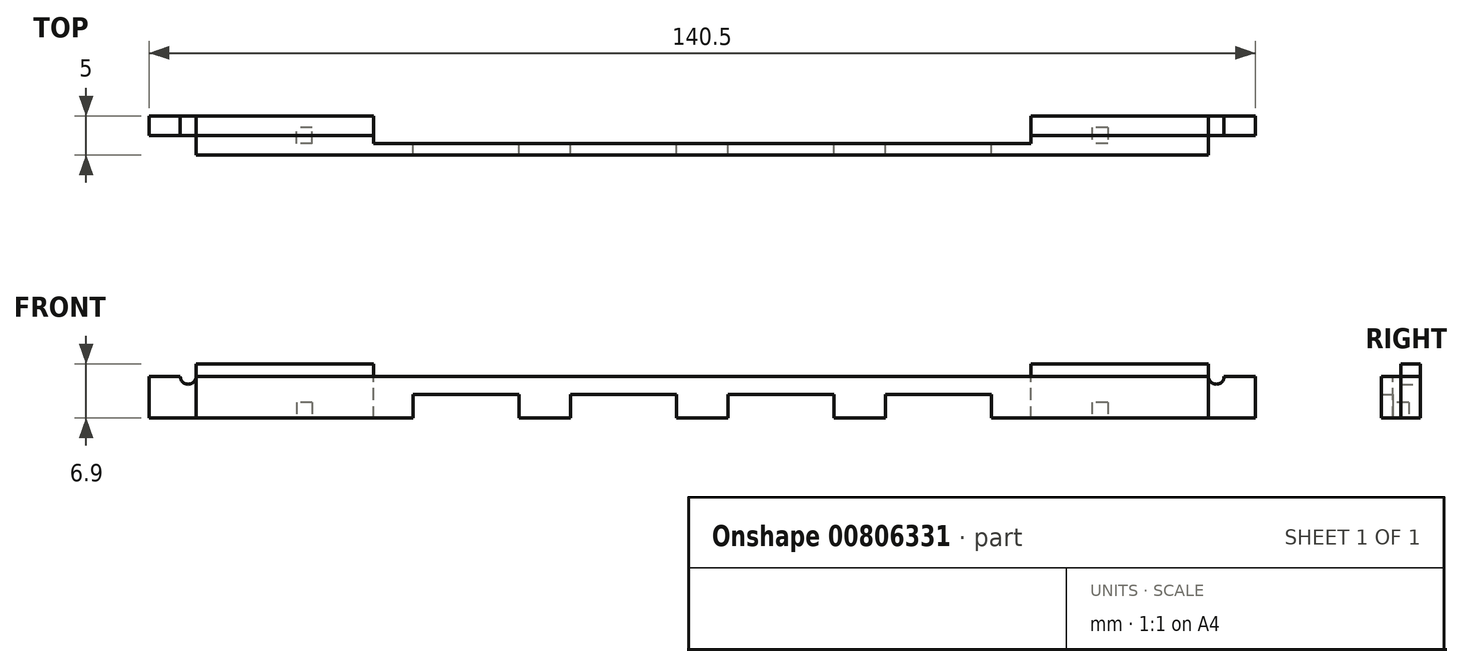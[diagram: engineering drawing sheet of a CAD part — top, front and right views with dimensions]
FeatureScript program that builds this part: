
annotation { "Feature Type Name" : "Feature", "Feature Type Description" : "" }
export const myFeature = defineFeature(function(context is Context, id is Id, definition is map)
    precondition{}
    {
        {
            var Q0;
            Q0=qCreatedBy(makeId("Front.planeOp"),FACE);
            var sketch = newSketch(context, id + "F0", { "sketchPlane" : qUnion([Q0])});
            skLineSegment(sketch, "E0.bottom", {"start": v(64.3, 7.08) * mm, "end": v(-64.3, 7.08) * mm});
            skLineSegment(sketch, "E0.left", {"start": v(64.3, 7.08) * mm, "end": v(64.3, -6.72) * mm});
            skLineSegment(sketch, "E0.right", {"start": v(-64.3, 7.08) * mm, "end": v(-64.3, -6.72) * mm});
            skPoint(sketch, "E0.middle", {"position": v(0, 0.18) * mm});
            skLineSegment(sketch, "E1.top", {"start": v(-70.25, 5.48) * mm, "end": v(70.25, 5.48) * mm});
            skLineSegment(sketch, "E1.left", {"start": v(-70.25, -6.72) * mm, "end": v(-70.25, 5.48) * mm});
            skLineSegment(sketch, "E1.right", {"start": v(70.25, -6.72) * mm, "end": v(70.25, 5.48) * mm});
            skCircle(sketch, "E2", {"center": v(65.3, 5.48) * mm, "radius": 1 * mm});
            skCircle(sketch, "E3", {"center": v(-65.3, 5.48) * mm, "radius": 1 * mm});
            skLineSegment(sketch, "E4.bottom", {"start": v(-23.25, 3.18) * mm, "end": v(-36.75, 3.18) * mm});
            skLineSegment(sketch, "E4.left", {"start": v(-23.25, 3.18) * mm, "end": v(-23.25, -2.82) * mm});
            skLineSegment(sketch, "E4.right", {"start": v(-36.75, 3.18) * mm, "end": v(-36.75, -2.82) * mm});
            skPoint(sketch, "E4.middle", {"position": v(-30, 0.18) * mm});
            skLineSegment(sketch, "E5.bottom", {"start": v(-3.25, 3.18) * mm, "end": v(-16.75, 3.18) * mm});
            skLineSegment(sketch, "E5.left", {"start": v(-3.25, 3.18) * mm, "end": v(-3.25, -2.82) * mm});
            skLineSegment(sketch, "E5.right", {"start": v(-16.75, 3.18) * mm, "end": v(-16.75, -2.82) * mm});
            skPoint(sketch, "E5.middle", {"position": v(-10, 0.18) * mm});
            skLineSegment(sketch, "E6.bottom", {"start": v(16.75, 3.18) * mm, "end": v(3.25, 3.18) * mm});
            skLineSegment(sketch, "E6.left", {"start": v(16.75, 3.18) * mm, "end": v(16.75, -2.82) * mm});
            skLineSegment(sketch, "E6.right", {"start": v(3.25, 3.18) * mm, "end": v(3.25, -2.82) * mm});
            skPoint(sketch, "E6.middle", {"position": v(10, 0.18) * mm});
            skLineSegment(sketch, "E7.bottom", {"start": v(36.75, 3.18) * mm, "end": v(23.25, 3.18) * mm});
            skLineSegment(sketch, "E7.left", {"start": v(36.75, 3.18) * mm, "end": v(36.75, -2.82) * mm});
            skLineSegment(sketch, "E7.right", {"start": v(23.25, 3.18) * mm, "end": v(23.25, -2.82) * mm});
            skPoint(sketch, "E7.middle", {"position": v(30, 0.18) * mm});
            skPoint(sketch, "E8", {"position": v(-36.75, 0.18) * mm});
            skPoint(sketch, "E9", {"position": v(36.75, 0.18) * mm});
            skPoint(sketch, "E10", {"position": v(-70.25, 0.18) * mm});
            skPoint(sketch, "E11", {"position": v(70.25, 0.18) * mm});
            skLineSegment(sketch, "E12", {"start": v(-70.25, 0.18) * mm, "end": v(70.25, 0.18) * mm});
            skSolve(sketch);
        }
        {
            var Q0;
            {var subQ8=sQuery(id+"F0.wireOp",EDGE,"E4.bottom");Q0=makeQuery(id+"F0.imprint","IMPRINT",FACE,{"disambiguationData":[TD([[makeQuery(id+"F0.imprint","IMPRINT",EDGE,{"derivedFrom":subQ8}),-1.0]])]});}
            extrude(context, id + "F1", {"entities" : qUnion([Q0]), "depth" : 5 * mm, "offsetDistance" : 25 * mm});
        }
        {
            var Q0;
            {var subQ1=sQuery(id+"F0.wireOp",EDGE,"E1.top");var subQ7=sQuery(id+"F0.wireOp",EDGE,"E1.left");var subQ8=makeQuery(id+"F0.imprint","INTERSECT",VERTEX,{"derivedFrom":[subQ1,subQ7]});Q0=makeQuery(id+"F0.imprint","IMPRINT",FACE,{"disambiguationData":[TD([[makeQuery(id+"F0.imprint","IMPRINT",EDGE,{"disambiguationData":[TD([[subQ8,-1.0]])],"derivedFrom":subQ1}),-1.0]])]});}
            var Q1;
            {var subQ0=sQuery(id+"F0.wireOp",EDGE,"E0.bottom");Q1=makeQuery(id+"F0.imprint","IMPRINT",FACE,{"disambiguationData":[TD([[makeQuery(id+"F0.imprint","IMPRINT",EDGE,{"derivedFrom":subQ0}),1.0]])]});}
            var Q2;
            {var subQ1=sQuery(id+"F0.wireOp",EDGE,"E1.top");var subQ7=sQuery(id+"F0.wireOp",EDGE,"E1.right");var subQ8=makeQuery(id+"F0.imprint","INTERSECT",VERTEX,{"derivedFrom":[subQ1,subQ7]});Q2=makeQuery(id+"F0.imprint","IMPRINT",FACE,{"disambiguationData":[TD([[makeQuery(id+"F0.imprint","IMPRINT",EDGE,{"disambiguationData":[TD([[subQ8,1.0]])],"derivedFrom":subQ1}),-1.0]])]});}
            extrude(context, id + "F2", {"entities" : qUnion([Q0, Q1, Q2]), "operationType" : NewBodyOperationType.ADD, "depth" : 2.5 * mm, "offsetDistance" : 25 * mm});
        }
        {
            var Q0;
            {var subQ0=sQuery(id+"F0.wireOp",EDGE,"E12");var subQ1=makeQuery(id+"F0.imprint","INTERSECT",VERTEX,{"derivedFrom":[sQuery(id+"F0.wireOp",EDGE,"E0.left"),subQ0]});Q0=makeQuery(id+"F2.boolean.opBoolean","MERGE",FACE,{"derivedFrom":[makeQuery(id+"F1.opExtrude","SWEPT_FACE",FACE,{"disambiguationData":[OSD([subQ0]),TDD([makeQuery(id+"F0.imprint","IMPRINT",EDGE,{"disambiguationData":[TD([[subQ1,1.0]])],"derivedFrom":subQ0})])]}),makeQuery(id+"F2.opExtrude","SWEPT_FACE",FACE,{"disambiguationData":[OSD([subQ0]),TDD([makeQuery(id+"F0.imprint","IMPRINT",EDGE,{"disambiguationData":[TD([[makeQuery(id+"F0.imprint","INTERSECT",VERTEX,{"derivedFrom":[sQuery(id+"F0.wireOp",EDGE,"E1.right"),subQ0]}),1.0]])],"derivedFrom":subQ0})])]})]});}
            var sketch = newSketch(context, id + "F3", { "sketchPlane" : qUnion([Q0])});
            skLineSegment(sketch, "E13", {"start": v(50.52, 5) * mm, "end": v(50.52, 0) * mm, "construction": true});
            skPoint(sketch, "E14", {"position": v(50.52, 2.5) * mm});
            skLineSegment(sketch, "E15.bottom", {"start": v(51.52, 1.5) * mm, "end": v(49.52, 1.5) * mm});
            skLineSegment(sketch, "E15.top", {"start": v(51.52, 3.5) * mm, "end": v(49.52, 3.5) * mm});
            skLineSegment(sketch, "E15.left", {"start": v(51.52, 1.5) * mm, "end": v(51.52, 3.5) * mm});
            skLineSegment(sketch, "E15.right", {"start": v(49.52, 1.5) * mm, "end": v(49.52, 3.5) * mm});
            skSolve(sketch);
        }
        {
            var Q0;
            Q0=makeQuery(id+"F3.imprint","IMPRINT",FACE,{"disambiguationData":[TD([[makeQuery(id+"F3.imprint","IMPRINT",EDGE,{"derivedFrom":sQuery(id+"F3.wireOp",EDGE,"E15.bottom")}),-1.0]])]});
            extrude(context, id + "F4", {"entities" : qUnion([Q0]), "operationType" : NewBodyOperationType.REMOVE, "oppositeDirection" : true, "depth" : 2 * mm, "offsetDistance" : 25 * mm});
        }
        {
            var Q0;
            {var subQ0=sQuery(id+"F0.wireOp",EDGE,"E12");var subQ1=makeQuery(id+"F0.imprint","INTERSECT",VERTEX,{"derivedFrom":[sQuery(id+"F0.wireOp",EDGE,"E0.right"),subQ0]});Q0=makeQuery(id+"F2.boolean.opBoolean","MERGE",FACE,{"derivedFrom":[makeQuery(id+"F1.opExtrude","SWEPT_FACE",FACE,{"disambiguationData":[OSD([subQ0]),TDD([makeQuery(id+"F0.imprint","IMPRINT",EDGE,{"disambiguationData":[TD([[subQ1,-1.0]])],"derivedFrom":subQ0})])]}),makeQuery(id+"F2.opExtrude","SWEPT_FACE",FACE,{"disambiguationData":[OSD([subQ0]),TDD([makeQuery(id+"F0.imprint","IMPRINT",EDGE,{"disambiguationData":[TD([[makeQuery(id+"F0.imprint","INTERSECT",VERTEX,{"derivedFrom":[sQuery(id+"F0.wireOp",EDGE,"E1.left"),subQ0]}),-1.0]])],"derivedFrom":subQ0})])]})]});}
            var sketch = newSketch(context, id + "F5", { "sketchPlane" : qUnion([Q0])});
            skLineSegment(sketch, "E16", {"start": v(-50.52, 5) * mm, "end": v(-50.52, 0) * mm, "construction": true});
            skPoint(sketch, "E17", {"position": v(-50.52, 2.5) * mm});
            skLineSegment(sketch, "E18.bottom", {"start": v(-49.52, 3.5) * mm, "end": v(-51.52, 3.5) * mm});
            skLineSegment(sketch, "E18.top", {"start": v(-49.52, 1.5) * mm, "end": v(-51.52, 1.5) * mm});
            skLineSegment(sketch, "E18.left", {"start": v(-49.52, 3.5) * mm, "end": v(-49.52, 1.5) * mm});
            skLineSegment(sketch, "E18.right", {"start": v(-51.52, 3.5) * mm, "end": v(-51.52, 1.5) * mm});
            skSolve(sketch);
        }
        {
            var Q0;
            Q0=makeQuery(id+"F5.imprint","IMPRINT",FACE,{"disambiguationData":[TD([[makeQuery(id+"F5.imprint","IMPRINT",EDGE,{"derivedFrom":sQuery(id+"F5.wireOp",EDGE,"E18.bottom")}),1.0]])]});
            extrude(context, id + "F6", {"entities" : qUnion([Q0]), "operationType" : NewBodyOperationType.REMOVE, "oppositeDirection" : true, "depth" : 2 * mm, "offsetDistance" : 25 * mm});
        }
        {
            var Q0;
            {var subQ0=sQuery(id+"F0.wireOp",EDGE,"E12");var subQ1=sQuery(id+"F0.wireOp",EDGE,"E1.top");var subQ2=sQuery(id+"F0.wireOp",EDGE,"E0.right");var subQ3=sQuery(id+"F0.wireOp",EDGE,"E0.left");Q0=makeQuery(id+"F2.boolean.opBoolean","MERGE",FACE,{"derivedFrom":[makeQuery(id+"F1.opExtrude","CAP_FACE",FACE,{"disambiguationData":[OSD([subQ3,subQ2,subQ1,sQuery(id+"F0.wireOp",EDGE,"E4.bottom"),sQuery(id+"F0.wireOp",EDGE,"E4.left"),sQuery(id+"F0.wireOp",EDGE,"E4.right"),sQuery(id+"F0.wireOp",EDGE,"E5.bottom"),sQuery(id+"F0.wireOp",EDGE,"E5.left"),sQuery(id+"F0.wireOp",EDGE,"E5.right"),sQuery(id+"F0.wireOp",EDGE,"E6.bottom"),sQuery(id+"F0.wireOp",EDGE,"E6.left"),sQuery(id+"F0.wireOp",EDGE,"E6.right"),sQuery(id+"F0.wireOp",EDGE,"E7.bottom"),sQuery(id+"F0.wireOp",EDGE,"E7.left"),sQuery(id+"F0.wireOp",EDGE,"E7.right"),subQ0])],"isStart":true}),makeQuery(id+"F2.opExtrude","CAP_FACE",FACE,{"disambiguationData":[OSD([sQuery(id+"F0.wireOp",EDGE,"E0.bottom"),subQ3,subQ2,subQ1])],"isStart":true}),makeQuery(id+"F2.opExtrude","CAP_FACE",FACE,{"disambiguationData":[OSD([subQ3,subQ1,sQuery(id+"F0.wireOp",EDGE,"E1.right"),sQuery(id+"F0.wireOp",EDGE,"E2"),subQ0])],"isStart":true}),makeQuery(id+"F2.opExtrude","CAP_FACE",FACE,{"disambiguationData":[OSD([subQ2,subQ1,sQuery(id+"F0.wireOp",EDGE,"E1.left"),sQuery(id+"F0.wireOp",EDGE,"E3"),subQ0])],"isStart":true})]});}
            var sketch = newSketch(context, id + "F7", { "sketchPlane" : qUnion([Q0])});
            skPoint(sketch, "E19", {"position": v(-41.75, 0.18) * mm});
            skPoint(sketch, "E20", {"position": v(41.75, 0.18) * mm});
            skLineSegment(sketch, "E21", {"start": v(-70.25, 5.48) * mm, "end": v(70.25, 5.48) * mm, "construction": true});
            skLineSegment(sketch, "E22.bottom", {"start": v(-41.75, 0.18) * mm, "end": v(41.75, 0.18) * mm});
            skLineSegment(sketch, "E22.top", {"start": v(-41.75, 7.18) * mm, "end": v(41.75, 7.18) * mm});
            skLineSegment(sketch, "E22.left", {"start": v(-41.75, 0.18) * mm, "end": v(-41.75, 7.18) * mm});
            skLineSegment(sketch, "E22.right", {"start": v(41.75, 0.18) * mm, "end": v(41.75, 7.18) * mm});
            skSolve(sketch);
        }
        {
            var Q0;
            Q0=makeQuery(id+"F7.imprint","IMPRINT",FACE,{"disambiguationData":[TD([[makeQuery(id+"F7.imprint","IMPRINT",EDGE,{"derivedFrom":makeQuery(id+"F1.opExtrude","CAP_EDGE",EDGE,{"disambiguationData":[OSD([sQuery(id+"F0.wireOp",EDGE,"E4.bottom")])],"isStart":true})}),1.0]])]});
            extrude(context, id + "F8", {"entities" : qUnion([Q0]), "operationType" : NewBodyOperationType.REMOVE, "oppositeDirection" : true, "depth" : 3.5 * mm, "offsetDistance" : 25 * mm});
        }
    });
